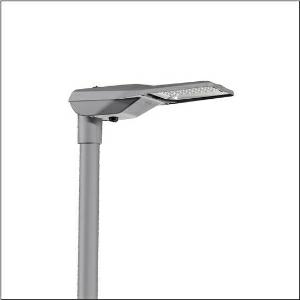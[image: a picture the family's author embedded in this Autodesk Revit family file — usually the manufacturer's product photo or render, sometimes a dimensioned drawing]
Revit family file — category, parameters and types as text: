
# Revit family: streetlight_sl_21_mini___p0_5a_5xe2v33t08jb_709b
name_source: partatom
category: Lighting Fixtures
units: mm (PartAtom-declared; Revit-internal decimal feet)

## family parameters
Cut with Voids When Loaded = No
Host = Face
Light Source = No
Part Type = Normal
Room Calculation Point = No
Round Connector Dimension = Use Diameter
Shared = No

## types (1)
- --- (1 x LED, 12720 lm, 88.6 W, 3000K)
    Apparent Load = 89 VA
    CIE Flux Codes = 37 73 96 100 100
    Color Rendering = 70
    Color Temperature = 3000K
    Default Elevation = 1800 mm
    Description = Streetlight SL 21 mini, mast luminaire, primary light control with lens, of PMMA, primary optical cover: cover, of toughened safety glass, transparent, light distribution: P0.5a, light emission: direct distribution, primary light characteristic: asymmetric, installation type: post-top, side-entry, LED, High Power LED, rated luminous flux: 12.720lm, luminous efficacy: 144lm/W, light colour: 730, colour temperature: 3000K, control gear: D4i, control: pre-setting: logarithmic dimming characteristic, flexible luminous flux parameterisation, time-dependent luminous flux control, constant luminous flux control, overheat protection, mains connection: 220..240V, AC, 50/60Hz, start of lifetime: 89W, end of service life: 92W, reduction: 41W, luminaire housing, of diecast aluminium, powder-coated, Siteco® metallic grey (DB 702S), corrosivity category C5 mid according to DIN EN ISO 12944, multi-level sealing system, sealing non-destructively replaceable, inclination adjustable: 0°, 5°, 10°, 15°, please order mast flange separately, length: 628mm, width: 235mm, height: 110mm, mast flange for spigot size: 42mm (side-entry): 5XC10008XM4, 60/48mm (side-entry/post-top): 5XC10108XM2, 76/60mm (side-entry/post-top): 5XC10108XM1, mounting height: 4..8m, Smart Interface below and above, protection rating (complete): IP66, insulation class (complete): insulation class II (safety insulation), certification: CE, ENEC, ENEC+, VDE, impact resistance: IK10, permissible operating ambient temperature for outdoor applications: -40..+50°C, standard-compliant lighting for roads and squares, packaging unit: 1 piece

Light Distribution: P0.5a
    Height = 110 mm
    Lamp = 1 x LED
    Lamp Light Flux = 12720 lm
    Lamp Power = 88.6 W
    Lamp count = 1
    Length = 625 mm
    Luminous efficacy = 144 lm/W
    Manufacturer = Siteco
    ModVariant = No
    Model = 5XE2V33T08JB
    Number of Poles = 1
    OnlyDefault = Yes
    Power Factor = 1
    Product Name = Streetlight SL 21 mini | P0.5a
    Product group = mast luminaire | pylon top
    ProductGroupID = 6100
    Protection Class = Protection class II
    Protection Degree = IP 66
    RLX_Detail_Level = 1
    RLX_Emergency_Light_Flux = 0 lm
    RLX_Emergency_Type = 0
    RLX_Emergency_Type_DB = No
    RlxData = <blob elided: 26137 chars, md5=b188b17a>
    Socket = socket
    Standby Power = 0 W
    System Light Flux = 12720 lm
    System Power = 89 W
    Type Comments = factory setting: luminous flux: 100 % | dim-lin: 254 | 915 mA
    Type Image = l_1003514.jpg
    URL = http://relux.com
    VarID = @adj_032939
    Voltage = 0 V
    Weight = 0.00 kg
    Width = 234 mm

## geometry (parser evidence)
native form markers: Blend x4, Sweep x11
no freeform markers — native parametric forms only
